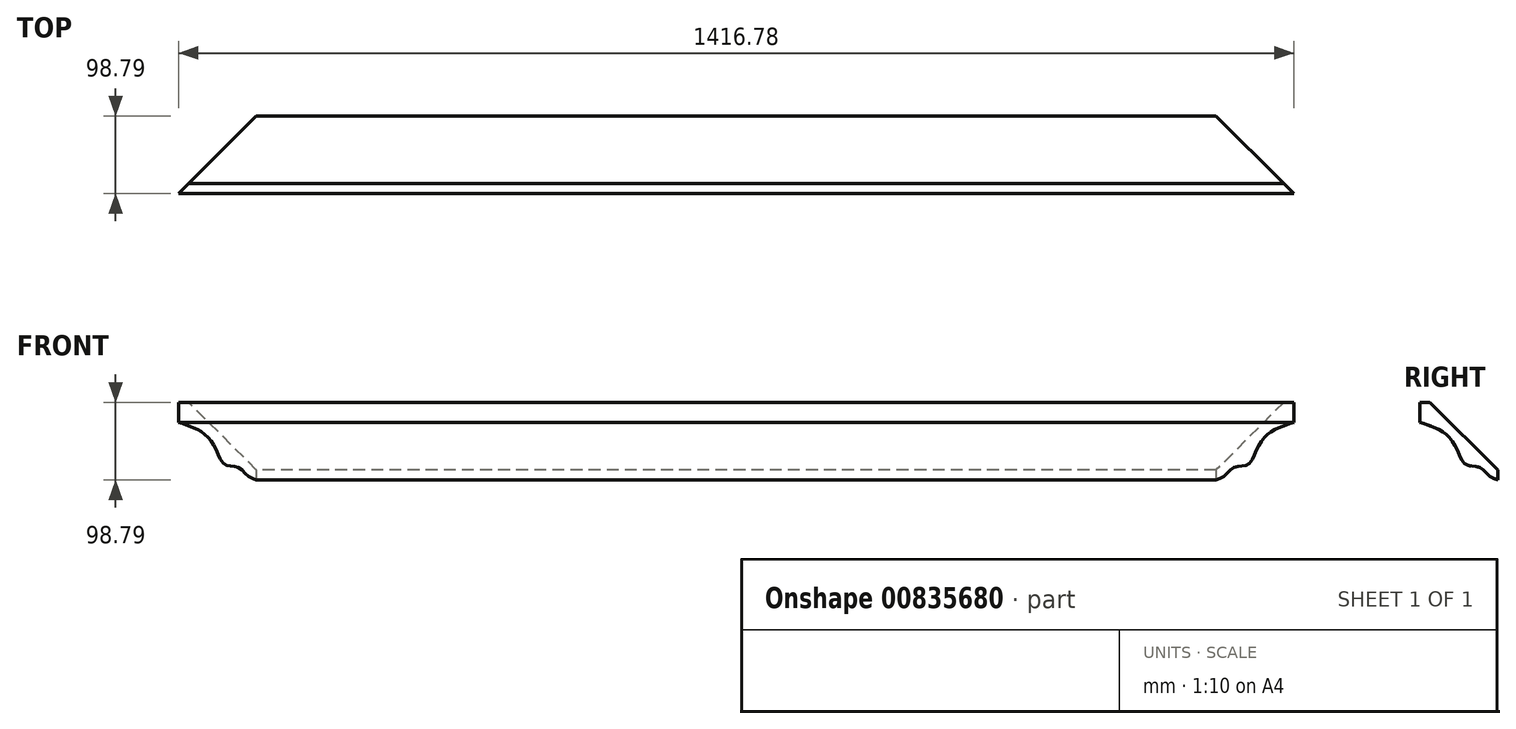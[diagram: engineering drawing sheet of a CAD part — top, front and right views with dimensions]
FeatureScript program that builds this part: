
annotation { "Feature Type Name" : "Feature", "Feature Type Description" : "" }
export const myFeature = defineFeature(function(context is Context, id is Id, definition is map)
    precondition{}
    {
        {
            var Q0;
            Q0=qCreatedBy(makeId("Right.planeOp"),FACE);
            var sketch = newSketch(context, id + "F0", { "sketchPlane" : qUnion([Q0])});
            skLineSegment(sketch, "E0", {"start": v(0, 0) * mm, "end": v(0, 12.7) * mm});
            skLineSegment(sketch, "E1", {"start": v(0, 12.7) * mm, "end": v(-86.09, 98.79) * mm});
            skLineSegment(sketch, "E2", {"start": v(-86.09, 98.79) * mm, "end": v(-98.79, 98.79) * mm});
            skLineSegment(sketch, "E3", {"start": v(-98.79, 98.79) * mm, "end": v(-98.79, 73.37) * mm});
            skFitSpline(sketch, "E4", {"points": [v(-98.79, 73.37) * mm, v(-67.03, 59.17) * mm, v(-50.62, 37.14) * mm, v(-40.3, 19.8) * mm, v(-22.03, 15.58) * mm, v(-12.19, 6.2) * mm, v(0, 0) * mm], "startDerivative": vector(161.42, -53.23) * mm, "endDerivative": vector(98.44, -35.45) * mm});
            skSolve(sketch);
        }
        {
            var Q0;
            Q0 = qSketchRegion(id + "F0", true);
            extrude(context, id + "F1", {"entities" : qUnion([Q0]), "depth" : 1447.8 * mm, "offsetDistance" : 25.4 * mm});
        }
        {
            var Q0;
            Q0=qCreatedBy(makeId("Top.planeOp"),FACE);
            var sketch = newSketch(context, id + "F2", { "sketchPlane" : qUnion([Q0])});
            skLineSegment(sketch, "E5", {"start": v(0, 0) * mm, "end": v(101.6, 0) * mm});
            skLineSegment(sketch, "E6", {"start": v(101.6, 0) * mm, "end": v(0, -101.6) * mm});
            skLineSegment(sketch, "E7", {"start": v(0, -101.6) * mm, "end": v(0, 0) * mm});
            skSolve(sketch);
        }
        {
            var Q0;
            Q0 = qSketchRegion(id + "F2", true);
            extrude(context, id + "F3", {"entities" : qUnion([Q0]), "operationType" : NewBodyOperationType.REMOVE, "depth" : 127 * mm, "offsetDistance" : 25.4 * mm});
        }
        {
            var Q0;
            Q0=qCreatedBy(makeId("Top.planeOp"),FACE);
            var sketch = newSketch(context, id + "F4", { "sketchPlane" : qUnion([Q0])});
            skLineSegment(sketch, "E8", {"start": v(1320.8, 0) * mm, "end": v(1542.45, 0) * mm});
            skLineSegment(sketch, "E9", {"start": v(1542.45, 0) * mm, "end": v(1542.45, -221.65) * mm});
            skLineSegment(sketch, "E10", {"start": v(1542.45, -221.65) * mm, "end": v(1320.8, 0) * mm});
            skSolve(sketch);
        }
        {
            var Q0;
            Q0 = qSketchRegion(id + "F4", true);
            extrude(context, id + "F5", {"entities" : qUnion([Q0]), "operationType" : NewBodyOperationType.REMOVE, "depth" : 127 * mm, "offsetDistance" : 25.4 * mm});
        }
    });
